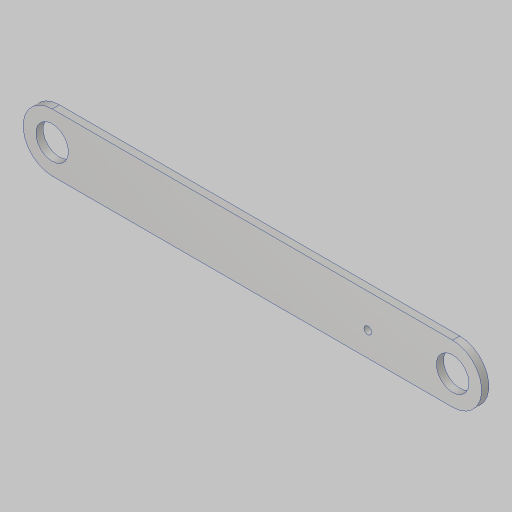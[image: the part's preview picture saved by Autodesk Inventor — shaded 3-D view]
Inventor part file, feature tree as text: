
AUTODESK INVENTOR PART (.ipt)
format: ipt  version: 2023.5 (Build 275446000, 446)  size: 108,032 bytes
history: native  units: in
note: dims shown in document units (in); Inventor stores cm internally (conversion verified against a paired STEP export)
features: sketch x2, extrude x1, hole x1
ambient origin geometry x8: Origin, YZ Plane, XZ Plane, XY Plane, X Axis, Y Axis, Z Axis, Center Point
bodies: Solid1 (feature_tree)
feature tree (4):
  extrude  "Extrusion1"  Depth=13.795in
  hole  "Hole1"  [1 undecoded]
  sketch  "Sketch1"  dims[d0=1.125in d1=13.795in]
  sketch  "Sketch2"  dims[d2=2.0in d3=0.25in d4=0.0in d6=0.266in d7=0.5in d8=0.507in d9=0.25in d10=0.5635in d11=0.75in d12=0.8108in d13=0.167in d14=10.875in]
note: 1 required parameter value undecoded (feature->parameter linkage not recoverable at this tier; creation-order binding heuristic only, values carry confidence <= 0.55)
